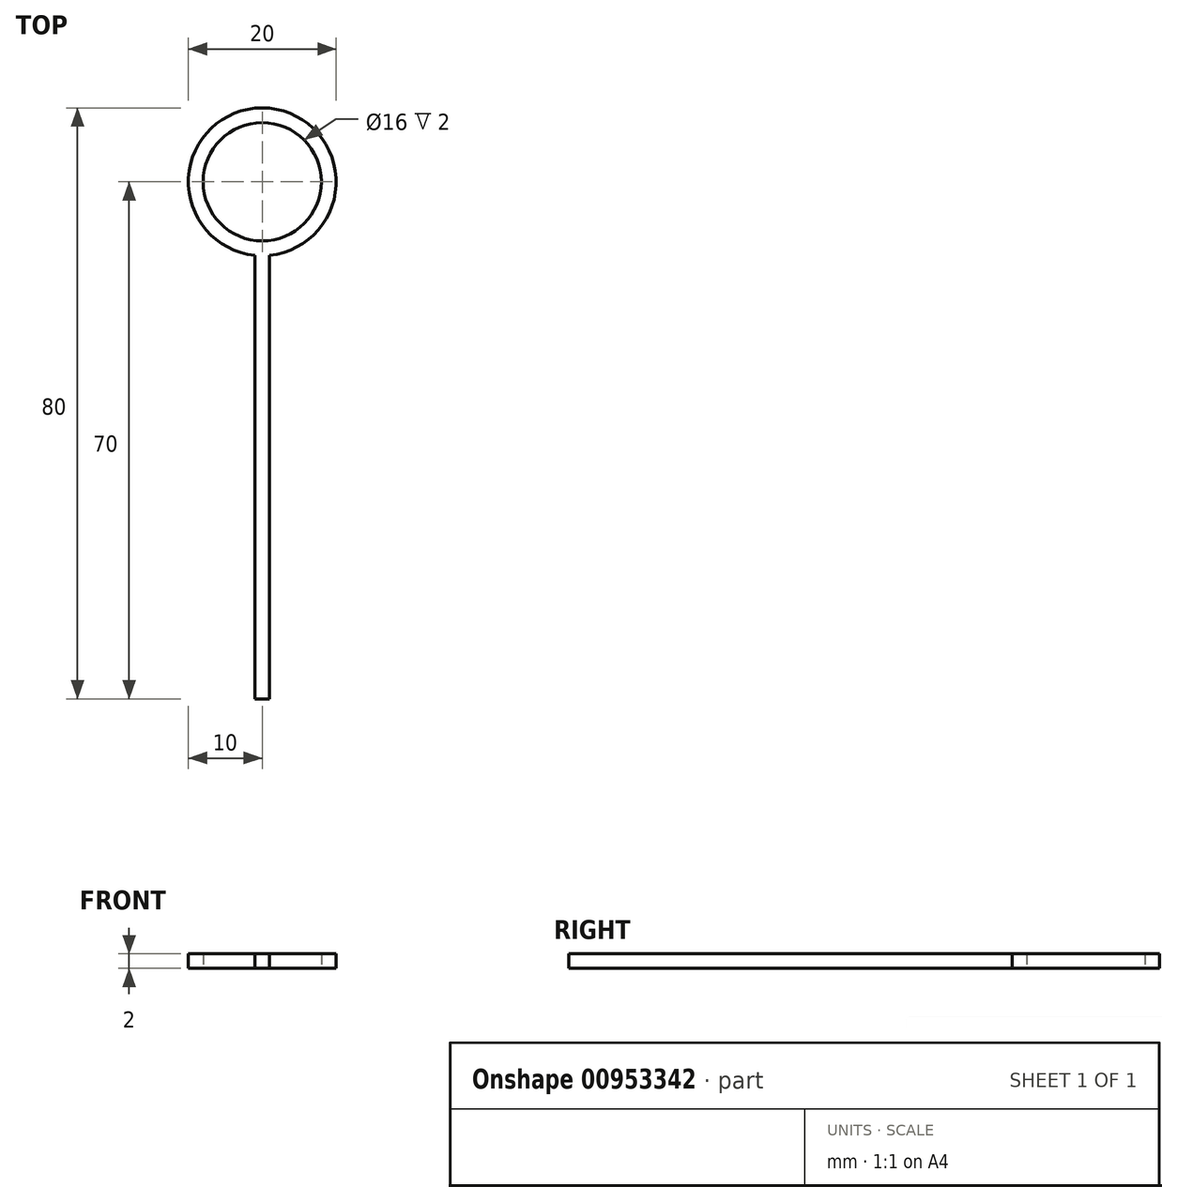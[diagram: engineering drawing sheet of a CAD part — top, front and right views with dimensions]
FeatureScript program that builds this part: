
annotation { "Feature Type Name" : "Feature", "Feature Type Description" : "" }
export const myFeature = defineFeature(function(context is Context, id is Id, definition is map)
    precondition{}
    {
        {
            var Q0;
            Q0=qCreatedBy(makeId("Top.planeOp"),FACE);
            var sketch = newSketch(context, id + "F0", { "sketchPlane" : qUnion([Q0])});
            skCircle(sketch, "E0", {"center": v(0, 0) * mm, "radius": 10 * mm});
            skCircle(sketch, "E1", {"center": v(0, 0) * mm, "radius": 8 * mm});
            skSolve(sketch);
        }
        {
            var Q0;
            Q0 = qSketchRegion(id + "F0", true);
            extrude(context, id + "F1", {"entities" : qUnion([Q0]), "depth" : 2 * mm, "offsetDistance" : 25 * mm});
        }
        {
            var Q0;
            Q0=qCreatedBy(makeId("Front.planeOp"),FACE);
            cPlane(context, id + "F2", {"entities" : qUnion([Q0]), "cplaneType" : CPlaneType.OFFSET, "offset" : 70 * mm, "width" : 150 * mm, "height" : 150 * mm});
        }
        {
            var Q0;
            Q0=qCreatedBy(id+"F2.planeOp",FACE);
            var sketch = newSketch(context, id + "F3", { "sketchPlane" : qUnion([Q0])});
            skLineSegment(sketch, "E2.bottom", {"start": v(-1, 2) * mm, "end": v(1, 2) * mm});
            skLineSegment(sketch, "E2.top", {"start": v(-1, 0) * mm, "end": v(1, 0) * mm});
            skLineSegment(sketch, "E2.left", {"start": v(-1, 2) * mm, "end": v(-1, 0) * mm});
            skLineSegment(sketch, "E2.right", {"start": v(1, 2) * mm, "end": v(1, 0) * mm});
            skPoint(sketch, "E2.middle", {"position": v(0, 1) * mm});
            skSolve(sketch);
        }
        {
            var Q0;
            Q0 = qSketchRegion(id + "F3", true);
            extrude(context, id + "F4", {"entities" : qUnion([Q0]), "operationType" : NewBodyOperationType.ADD, "endBound" : BoundingType.UP_TO_NEXT, "oppositeDirection" : true, "depth" : 25 * mm, "offsetDistance" : 25 * mm});
        }
    });
